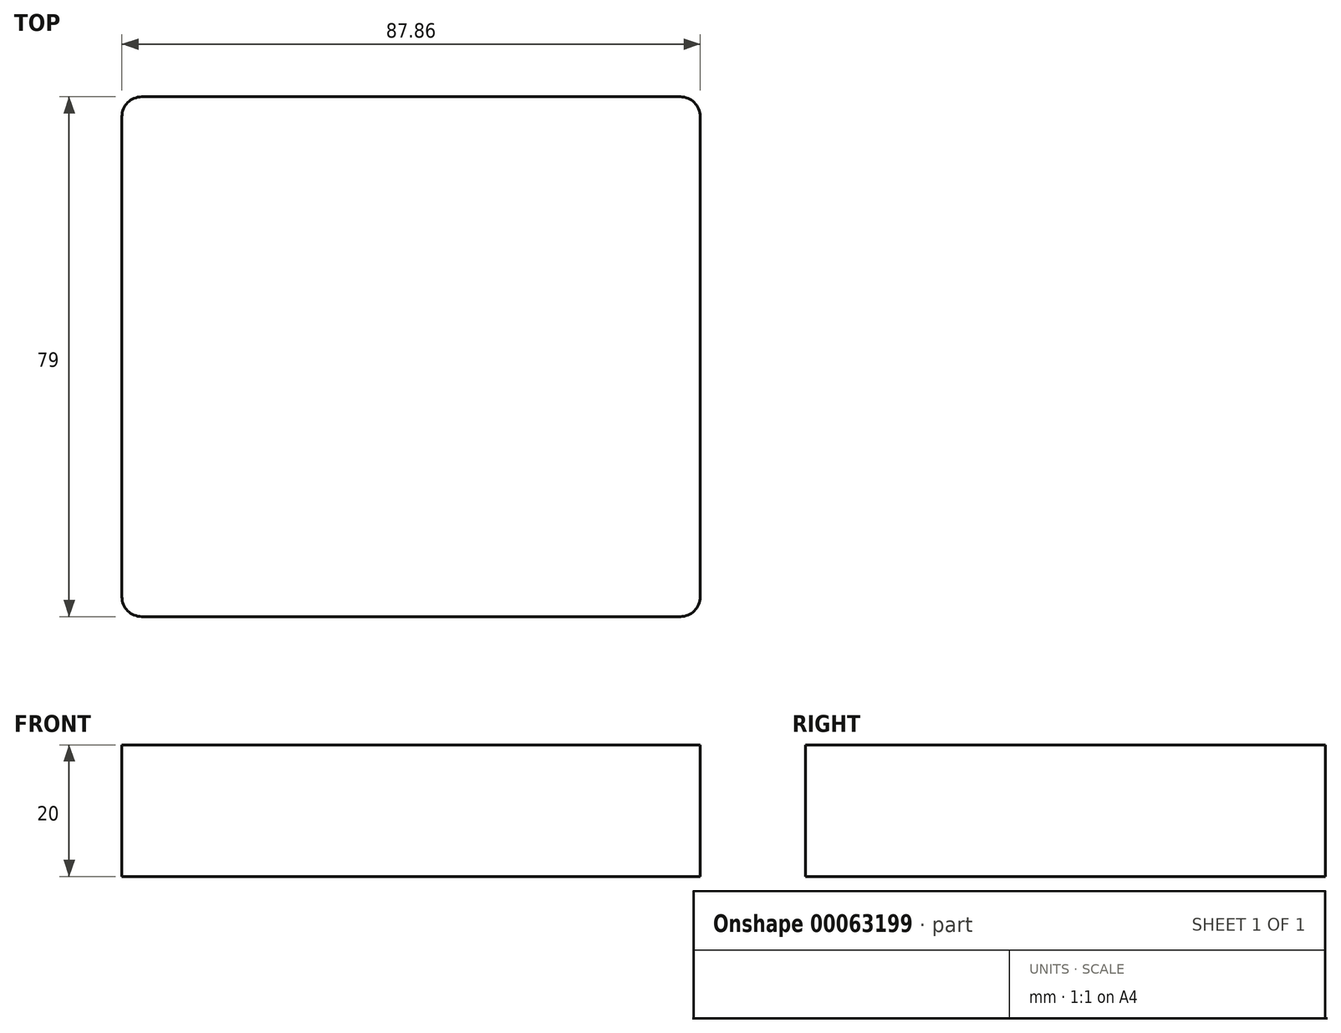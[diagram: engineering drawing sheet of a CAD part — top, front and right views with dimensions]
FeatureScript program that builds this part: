
annotation { "Feature Type Name" : "Feature", "Feature Type Description" : "" }
export const myFeature = defineFeature(function(context is Context, id is Id, definition is map)
    precondition{}
    {
        {
            var Q0;
            Q0=qCreatedBy(makeId("Top.planeOp"),FACE);
            var sketch = newSketch(context, id + "F0", { "sketchPlane" : qUnion([Q0])});
            skLineSegment(sketch, "E0.rect.bottom", {"start": v(43.93, -39.5) * mm, "end": v(-43.93, -39.5) * mm});
            skLineSegment(sketch, "E0.rect.top", {"start": v(43.93, 39.5) * mm, "end": v(-43.93, 39.5) * mm});
            skLineSegment(sketch, "E0.rect.left", {"start": v(43.93, -39.5) * mm, "end": v(43.93, 39.5) * mm});
            skLineSegment(sketch, "E0.rect.right", {"start": v(-43.93, -39.5) * mm, "end": v(-43.93, 39.5) * mm});
            skPoint(sketch, "E0.rect.middle", {"position": v(0, 0) * mm});
            skSolve(sketch);
        }
        {
            var Q0;
            Q0=makeQuery(id+"F0.imprint","IMPRINT",FACE,{"disambiguationData":[TD([[makeQuery(id+"F0.imprint","IMPRINT",EDGE,{"derivedFrom":sQuery(id+"F0.wireOp",EDGE,"E0.rect.bottom")}),-1.0]])]});
            extrude(context, id + "F1", {"entities" : qUnion([Q0]), "depth" : 20 * mm});
        }
        {
            var Q0;
            Q0=makeQuery(id+"F1.opExtrude","SWEPT_EDGE",EDGE,{"disambiguationData":[OSD([sQuery(id+"F0.wireOp",EDGE,"E0.rect.bottom"),sQuery(id+"F0.wireOp",EDGE,"E0.rect.right")])]});
            var Q1;
            Q1=makeQuery(id+"F1.opExtrude","SWEPT_EDGE",EDGE,{"disambiguationData":[OSD([sQuery(id+"F0.wireOp",EDGE,"E0.rect.bottom"),sQuery(id+"F0.wireOp",EDGE,"E0.rect.left")])]});
            var Q2;
            Q2=makeQuery(id+"F1.opExtrude","SWEPT_EDGE",EDGE,{"disambiguationData":[OSD([sQuery(id+"F0.wireOp",EDGE,"E0.rect.top"),sQuery(id+"F0.wireOp",EDGE,"E0.rect.left")])]});
            fillet(context, id + "F2", {"entities" : qUnion([Q0, Q1, Q2]), "radius" : 3 * mm, "tangentPropagation" : true, "allowEdgeOverflow" : false});
        }
        {
            var Q0;
            Q0=makeQuery(id+"F1.opExtrude","SWEPT_EDGE",EDGE,{"disambiguationData":[OSD([sQuery(id+"F0.wireOp",EDGE,"E0.rect.top"),sQuery(id+"F0.wireOp",EDGE,"E0.rect.right")])]});
            fillet(context, id + "F3", {"entities" : qUnion([Q0]), "radius" : 3 * mm, "tangentPropagation" : true, "allowEdgeOverflow" : false});
        }
    });
